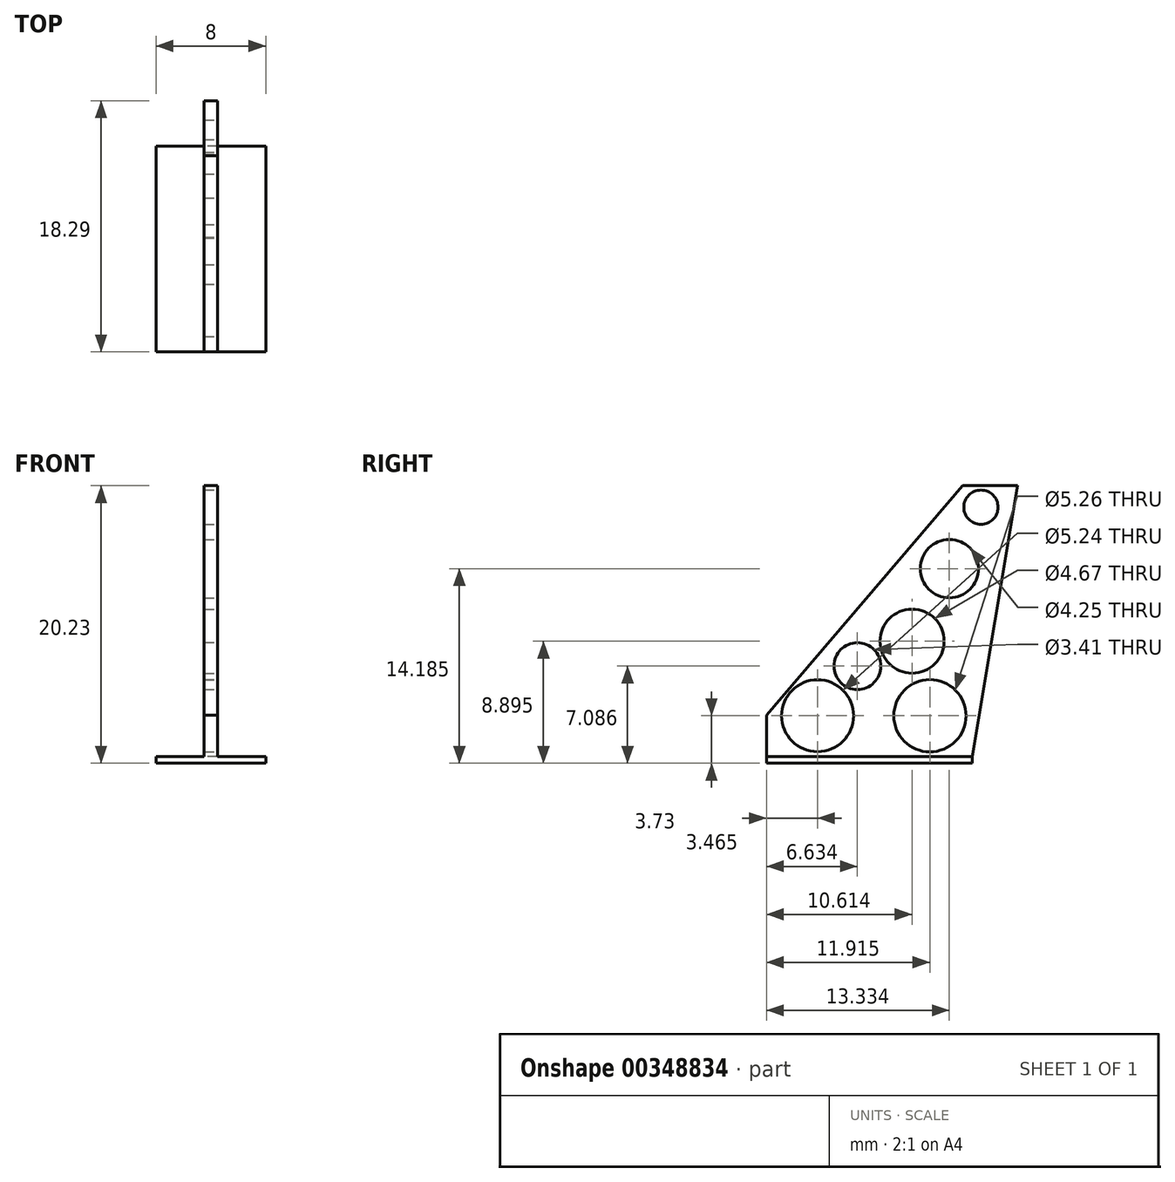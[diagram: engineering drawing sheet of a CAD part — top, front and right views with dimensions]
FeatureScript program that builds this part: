
annotation { "Feature Type Name" : "Feature", "Feature Type Description" : "" }
export const myFeature = defineFeature(function(context is Context, id is Id, definition is map)
    precondition{}
    {
        {
            var Q0;
            Q0=qCreatedBy(makeId("Right.planeOp"),FACE);
            var sketch = newSketch(context, id + "F0", { "sketchPlane" : qUnion([Q0])});
            skLineSegment(sketch, "E0", {"start": v(0, 0) * mm, "end": v(-15, 0) * mm});
            skLineSegment(sketch, "E1", {"start": v(-0.71, 19.73) * mm, "end": v(3.29, 19.73) * mm});
            skLineSegment(sketch, "E2", {"start": v(3.29, 19.73) * mm, "end": v(0, 0) * mm});
            skLineSegment(sketch, "E3", {"start": v(-15, 0) * mm, "end": v(-15, 3) * mm});
            skLineSegment(sketch, "E4", {"start": v(-15, 3) * mm, "end": v(-0.71, 19.73) * mm});
            skSolve(sketch);
        }
        {
            var Q0;
            Q0=makeQuery(id+"F0.imprint","IMPRINT",FACE,{"disambiguationData":[TD([[makeQuery(id+"F0.imprint","IMPRINT",EDGE,{"derivedFrom":sQuery(id+"F0.wireOp",EDGE,"E0")}),-1.0]])]});
            extrude(context, id + "F1", {"entities" : qUnion([Q0]), "endBound" : BoundingType.SYMMETRIC, "depth" : 1 * mm});
        }
        {
            var Q0;
            Q0=qCreatedBy(makeId("Right.planeOp"),FACE);
            var sketch = newSketch(context, id + "F2", { "sketchPlane" : qUnion([Q0])});
            skLineSegment(sketch, "E5.bottom", {"start": v(0, 0) * mm, "end": v(-15, 0) * mm});
            skLineSegment(sketch, "E5.top", {"start": v(0, -0.5) * mm, "end": v(-15, -0.5) * mm});
            skLineSegment(sketch, "E5.left", {"start": v(0, 0) * mm, "end": v(0, -0.5) * mm});
            skLineSegment(sketch, "E5.right", {"start": v(-15, 0) * mm, "end": v(-15, -0.5) * mm});
            skSolve(sketch);
        }
        {
            var Q0;
            Q0=makeQuery(id+"F2.imprint","IMPRINT",FACE,{"disambiguationData":[TD([[makeQuery(id+"F2.imprint","IMPRINT",EDGE,{"derivedFrom":sQuery(id+"F2.wireOp",EDGE,"E5.bottom")}),1.0]])]});
            extrude(context, id + "F3", {"entities" : qUnion([Q0]), "operationType" : NewBodyOperationType.ADD, "endBound" : BoundingType.SYMMETRIC, "depth" : 8 * mm});
        }
        {
            var Q0;
            Q0=makeQuery(id+"F1.opExtrude","CAP_FACE",FACE,{"disambiguationData":[OSD([sQuery(id+"F0.wireOp",EDGE,"E0"),sQuery(id+"F0.wireOp",EDGE,"E1"),sQuery(id+"F0.wireOp",EDGE,"E2"),sQuery(id+"F0.wireOp",EDGE,"E3"),sQuery(id+"F0.wireOp",EDGE,"E4")])],"isStart":false});
            var sketch = newSketch(context, id + "F4", { "sketchPlane" : qUnion([Q0])});
            skCircle(sketch, "E6", {"center": v(-11.27, 2.96) * mm, "radius": 2.62 * mm});
            skLineSegment(sketch, "E7", {"start": v(-11.27, 2.96) * mm, "end": v(-3.09, 2.96) * mm});
            skCircle(sketch, "E8", {"center": v(-3.09, 2.96) * mm, "radius": 2.63 * mm});
            skLineSegment(sketch, "E9", {"start": v(-7.18, 2.96) * mm, "end": v(0.63, 18.16) * mm});
            skCircle(sketch, "E10", {"center": v(-4.39, 8.4) * mm, "radius": 2.34 * mm});
            skCircle(sketch, "E11", {"center": v(0.63, 18.16) * mm, "radius": 1.25 * mm});
            skCircle(sketch, "E12", {"center": v(-1.67, 13.69) * mm, "radius": 2.13 * mm});
            skCircle(sketch, "E13", {"center": v(-8.57, 6.75) * mm, "radius": 1.4 * mm});
            skSolve(sketch);
        }
        {
            var Q0;
            Q0=makeQuery(id+"F4.imprint","IMPRINT",FACE,{"disambiguationData":[TD([[makeQuery(id+"F4.imprint","IMPRINT",EDGE,{"derivedFrom":sQuery(id+"F4.wireOp",EDGE,"E8")}),1.0]])]});
            var Q1;
            Q1=makeQuery(id+"F4.imprint","IMPRINT",FACE,{"disambiguationData":[TD([[makeQuery(id+"F4.imprint","IMPRINT",EDGE,{"derivedFrom":sQuery(id+"F4.wireOp",EDGE,"E6")}),1.0]])]});
            var Q2;
            {var subQ0=sQuery(id+"F4.wireOp",EDGE,"E10");var subQ1=sQuery(id+"F4.wireOp",EDGE,"E9");var subQ2=makeQuery(id+"F4.imprint","INTERSECT",VERTEX,{"disambiguationData":[OD(0.0)],"derivedFrom":[subQ1,subQ0]});Q2=makeQuery(id+"F4.imprint","IMPRINT",FACE,{"disambiguationData":[TD([[makeQuery(id+"F4.imprint","IMPRINT",EDGE,{"disambiguationData":[TD([[subQ2,-1.0]])],"derivedFrom":subQ1}),-1.0]])]});}
            var Q3;
            {var subQ0=sQuery(id+"F4.wireOp",EDGE,"E10");var subQ1=sQuery(id+"F4.wireOp",EDGE,"E9");var subQ2=makeQuery(id+"F4.imprint","INTERSECT",VERTEX,{"disambiguationData":[OD(0.0)],"derivedFrom":[subQ1,subQ0]});Q3=makeQuery(id+"F4.imprint","IMPRINT",FACE,{"disambiguationData":[TD([[makeQuery(id+"F4.imprint","IMPRINT",EDGE,{"disambiguationData":[TD([[subQ2,-1.0]])],"derivedFrom":subQ1}),1.0]])]});}
            var Q4;
            {var subQ0=sQuery(id+"F4.wireOp",EDGE,"E12");var subQ1=sQuery(id+"F4.wireOp",EDGE,"E9");var subQ2=makeQuery(id+"F4.imprint","INTERSECT",VERTEX,{"disambiguationData":[OD(0.0)],"derivedFrom":[subQ1,subQ0]});Q4=makeQuery(id+"F4.imprint","IMPRINT",FACE,{"disambiguationData":[TD([[makeQuery(id+"F4.imprint","IMPRINT",EDGE,{"disambiguationData":[TD([[subQ2,-1.0]])],"derivedFrom":subQ1}),-1.0]])]});}
            var Q5;
            {var subQ0=sQuery(id+"F4.wireOp",EDGE,"E12");var subQ1=sQuery(id+"F4.wireOp",EDGE,"E9");var subQ2=makeQuery(id+"F4.imprint","INTERSECT",VERTEX,{"disambiguationData":[OD(0.0)],"derivedFrom":[subQ1,subQ0]});Q5=makeQuery(id+"F4.imprint","IMPRINT",FACE,{"disambiguationData":[TD([[makeQuery(id+"F4.imprint","IMPRINT",EDGE,{"disambiguationData":[TD([[subQ2,-1.0]])],"derivedFrom":subQ1}),1.0]])]});}
            var Q6;
            Q6=makeQuery(id+"F4.imprint","IMPRINT",FACE,{"disambiguationData":[TD([[makeQuery(id+"F4.imprint","IMPRINT",EDGE,{"derivedFrom":sQuery(id+"F4.wireOp",EDGE,"E11")}),1.0]])]});
            extrude(context, id + "F5", {"entities" : qUnion([Q0, Q1, Q2, Q3, Q4, Q5, Q6]), "operationType" : NewBodyOperationType.REMOVE, "oppositeDirection" : true, "depth" : 25 * mm});
        }
        {
            var Q0;
            Q0=makeQuery(id+"F1.opExtrude","CAP_FACE",FACE,{"disambiguationData":[OSD([sQuery(id+"F0.wireOp",EDGE,"E0"),sQuery(id+"F0.wireOp",EDGE,"E1"),sQuery(id+"F0.wireOp",EDGE,"E2"),sQuery(id+"F0.wireOp",EDGE,"E3"),sQuery(id+"F0.wireOp",EDGE,"E4")])],"isStart":false});
            var sketch = newSketch(context, id + "F6", { "sketchPlane" : qUnion([Q0])});
            skCircle(sketch, "E14", {"center": v(-8.37, 6.59) * mm, "radius": 1.7 * mm});
            skSolve(sketch);
        }
        {
            var Q0;
            Q0=makeQuery(id+"F6.imprint","IMPRINT",FACE,{"disambiguationData":[TD([[makeQuery(id+"F6.imprint","IMPRINT",EDGE,{"derivedFrom":sQuery(id+"F6.wireOp",EDGE,"E14")}),1.0]])]});
            extrude(context, id + "F7", {"entities" : qUnion([Q0]), "operationType" : NewBodyOperationType.REMOVE, "oppositeDirection" : true, "depth" : 25 * mm});
        }
    });
